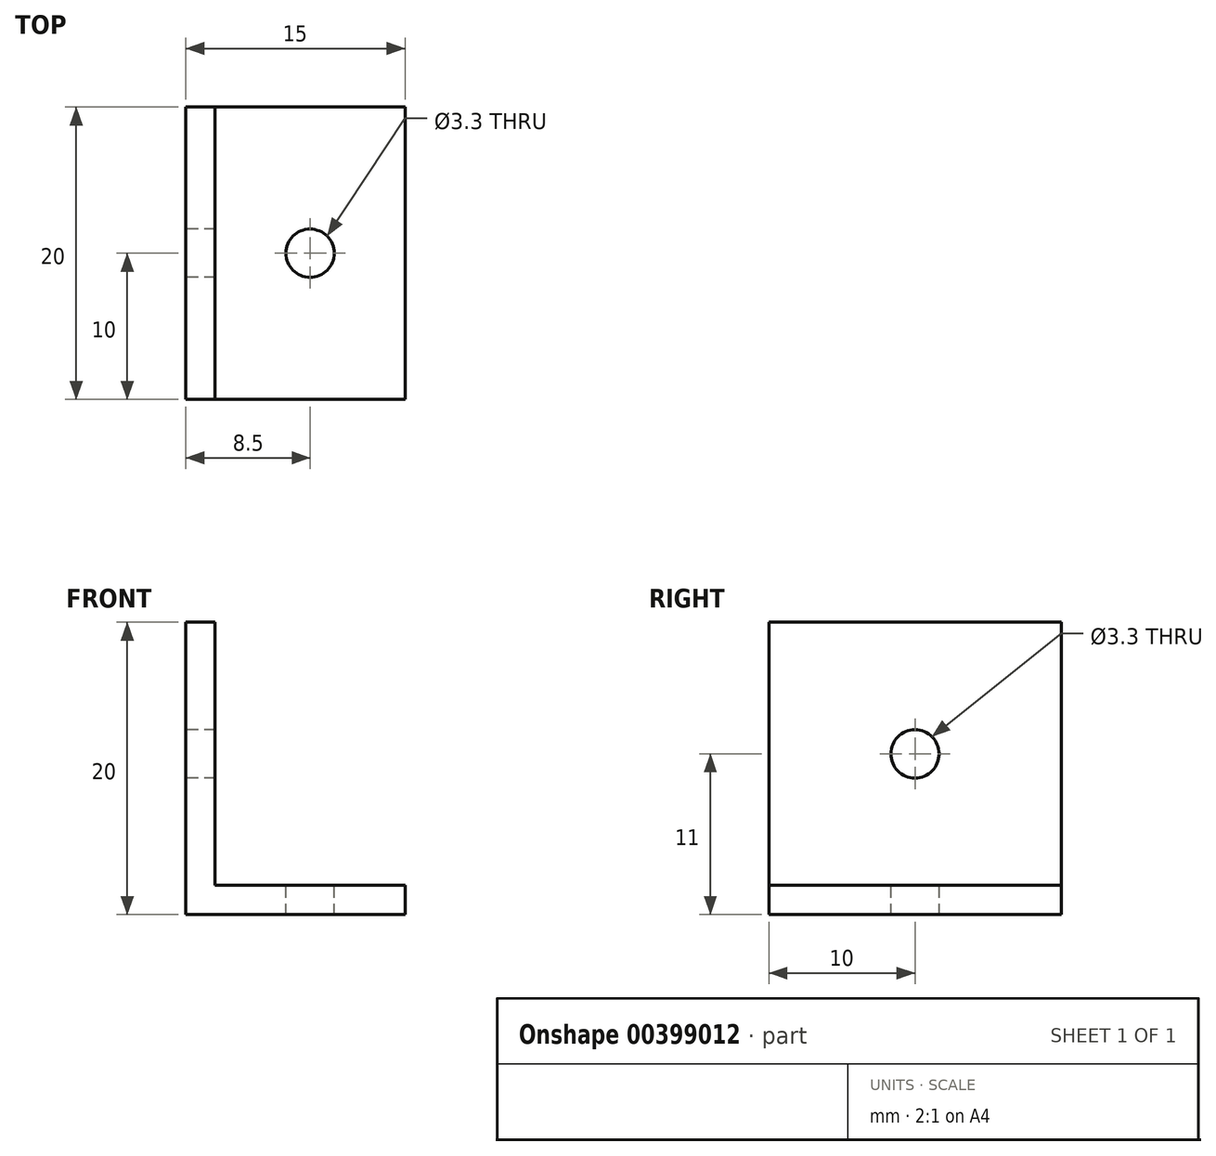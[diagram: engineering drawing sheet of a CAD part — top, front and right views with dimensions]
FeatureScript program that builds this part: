
annotation { "Feature Type Name" : "Feature", "Feature Type Description" : "" }
export const myFeature = defineFeature(function(context is Context, id is Id, definition is map)
    precondition{}
    {
        {
            var Q0;
            Q0=qCreatedBy(makeId("Front.planeOp"),FACE);
            var sketch = newSketch(context, id + "F0", { "sketchPlane" : qUnion([Q0])});
            skLineSegment(sketch, "E0", {"start": v(0, 0) * mm, "end": v(0, 20) * mm});
            skLineSegment(sketch, "E1", {"start": v(0, 20) * mm, "end": v(2, 20) * mm});
            skLineSegment(sketch, "E2", {"start": v(2, 20) * mm, "end": v(2, 2) * mm});
            skLineSegment(sketch, "E3", {"start": v(2, 2) * mm, "end": v(15, 2) * mm});
            skLineSegment(sketch, "E4", {"start": v(15, 2) * mm, "end": v(15, 0) * mm});
            skLineSegment(sketch, "E5", {"start": v(15, 0) * mm, "end": v(0, 0) * mm});
            skSolve(sketch);
        }
        {
            var Q0;
            Q0=makeQuery(id+"F0.imprint","IMPRINT",FACE,{"disambiguationData":[TD([[makeQuery(id+"F0.imprint","IMPRINT",EDGE,{"derivedFrom":sQuery(id+"F0.wireOp",EDGE,"E0")}),-1.0]])]});
            extrude(context, id + "F1", {"entities" : qUnion([Q0]), "depth" : 20 * mm, "symmetric" : true});
        }
        {
            var Q0;
            Q0=makeQuery(id+"F1.opExtrude","SWEPT_FACE",FACE,{"disambiguationData":[OSD([sQuery(id+"F0.wireOp",EDGE,"E0")])]});
            var sketch = newSketch(context, id + "F2", { "sketchPlane" : qUnion([Q0])});
            skLineSegment(sketch, "E6.0", {"start": v(10, 2) * mm, "end": v(-10, 2) * mm});
            skLineSegment(sketch, "E7.0", {"start": v(10, 20) * mm, "end": v(-10, 20) * mm});
            skLineSegment(sketch, "E8", {"start": v(0, 20) * mm, "end": v(0, 2) * mm, "construction": true});
            skPoint(sketch, "E9", {"position": v(0, 11) * mm});
            skSolve(sketch);
        }
        {
            var Q0;
            Q0=makeQuery(id+"F1.opExtrude","SWEPT_FACE",FACE,{"disambiguationData":[OSD([sQuery(id+"F0.wireOp",EDGE,"E3")])]});
            var sketch = newSketch(context, id + "F3", { "sketchPlane" : qUnion([Q0])});
            skLineSegment(sketch, "E10", {"start": v(2, 0) * mm, "end": v(15, 0) * mm, "construction": true});
            skPoint(sketch, "E11", {"position": v(8.5, 0) * mm});
            skSolve(sketch);
        }
        {
            var Q0;
            Q0=sQuery(id+"F2.wireOp",VERTEX,"E9");
            var Q1;
            Q1=sQuery(id+"F3.wireOp",VERTEX,"E11");
            var Q2;
            Q2=makeQuery(id+"F1.opExtrude","SWEPT_BODY",BODY,{"disambiguationData":[OSD([sQuery(id+"F0.wireOp",EDGE,"E0"),sQuery(id+"F0.wireOp",EDGE,"E1"),sQuery(id+"F0.wireOp",EDGE,"E2"),sQuery(id+"F0.wireOp",EDGE,"E3"),sQuery(id+"F0.wireOp",EDGE,"E4"),sQuery(id+"F0.wireOp",EDGE,"E5")])]});
            var Q3;
            Q3=makeQuery(id+"F1.opExtrude","SWEPT_BODY",BODY,{"disambiguationData":[OSD([sQuery(id+"F0.wireOp",EDGE,"E0"),sQuery(id+"F0.wireOp",EDGE,"E1"),sQuery(id+"F0.wireOp",EDGE,"E2"),sQuery(id+"F0.wireOp",EDGE,"E3"),sQuery(id+"F0.wireOp",EDGE,"E4"),sQuery(id+"F0.wireOp",EDGE,"E5")])]});
            hole(context, id + "F4", {"style" : HoleStyle.SIMPLE, "endStyle" : HoleEndStyle.THROUGH, "standardTappedOrClearance" : lookupTablePath({ "standard" : "ISO", "fit" : "Normal", "size" : "M3", "type" : "Clearance" }), "standardBlindInLast" : lookupTablePath({ "fit" : "Standard", "standard" : "ISO", "size" : "M3", "type" : "Clearance" }), "holeDiameter" : 3.3 * mm, "isTappedThrough" : true, "tappedDepth" : 3 * mm, "tapClearance" : 3, "locations" : qUnion([Q0, Q1]), "scope" : qUnion([Q2, Q3])});
        }
    });
